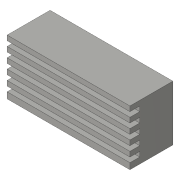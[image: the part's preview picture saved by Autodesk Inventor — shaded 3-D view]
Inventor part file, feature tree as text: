
AUTODESK INVENTOR PART (.ipt)
format: ipt  version: 2016 (Build 200138000, 138)  size: 104,448 bytes
history: native  units: in
note: dims shown in document units (in); Inventor stores cm internally (conversion verified against a paired STEP export)
features: extrude x2, sketch x2
ambient origin geometry x8: Origin, YZ Plane, XZ Plane, XY Plane, X Axis, Y Axis, Z Axis, Center Point
bodies: Solid1 (feature_tree)
feature tree (4):
  extrude  "Extrusion1"  Depth=1.125in
  extrude  "Extrusion2"  Depth=0.1in
  sketch  "Sketch1"  dims[d0=2.5in d1=1.125in]
  sketch  "Sketch2"  dims[d2=0.875in d3=0.0in d4=0.1in d5=0.1in d6=1.9685in d8=0.2in d9=0.3937in d11=1.0in d13=0.2in d14=0.0in]
